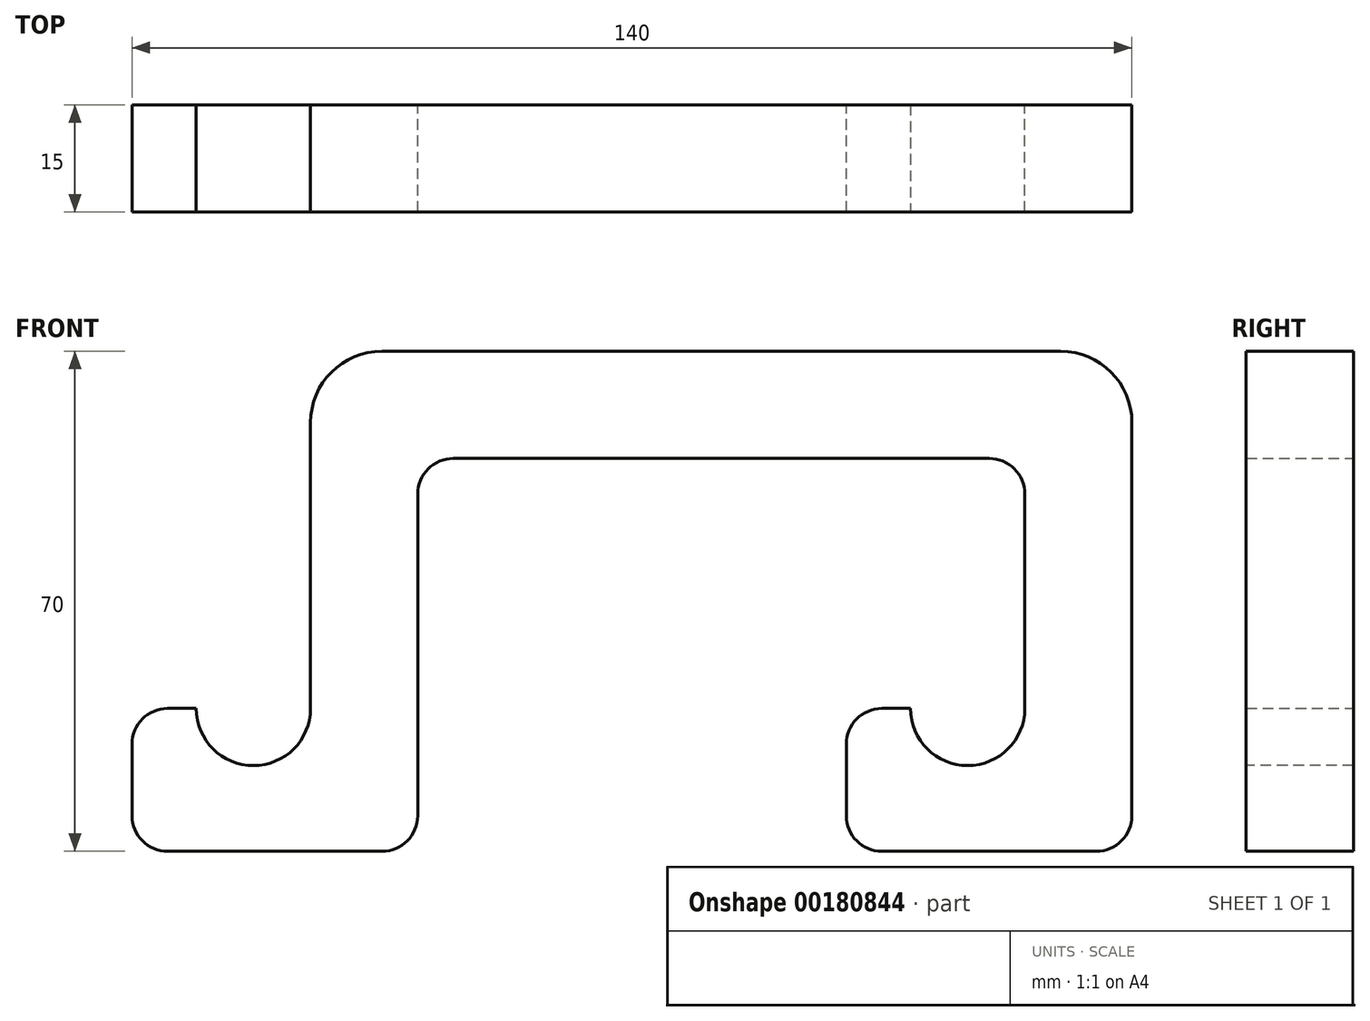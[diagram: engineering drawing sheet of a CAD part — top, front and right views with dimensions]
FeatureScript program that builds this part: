
annotation { "Feature Type Name" : "Feature", "Feature Type Description" : "" }
export const myFeature = defineFeature(function(context is Context, id is Id, definition is map)
    precondition{}
    {
        {
            var Q0;
            Q0=qCreatedBy(makeId("Front.planeOp"),FACE);
            var sketch = newSketch(context, id + "F0", { "sketchPlane" : qUnion([Q0])});
            skLineSegment(sketch, "E0", {"start": v(-64.65, 50) * mm, "end": v(50.35, 50) * mm});
            skLineSegment(sketch, "E1", {"start": v(50.35, 50) * mm, "end": v(50.35, -20) * mm});
            skLineSegment(sketch, "E2", {"start": v(50.35, -20) * mm, "end": v(10.35, -20) * mm});
            skLineSegment(sketch, "E3", {"start": v(10.35, 0) * mm, "end": v(35.35, 0) * mm});
            skLineSegment(sketch, "E4", {"start": v(35.35, 0) * mm, "end": v(35.35, 35) * mm});
            skLineSegment(sketch, "E5", {"start": v(35.35, 35) * mm, "end": v(-49.65, 35) * mm});
            skLineSegment(sketch, "E6", {"start": v(-49.65, 35) * mm, "end": v(-49.65, -20) * mm});
            skLineSegment(sketch, "E7", {"start": v(-49.65, -20) * mm, "end": v(-89.65, -20) * mm});
            skLineSegment(sketch, "E8", {"start": v(-89.65, 0) * mm, "end": v(-64.65, 0) * mm});
            skLineSegment(sketch, "E9", {"start": v(-64.65, 0) * mm, "end": v(-64.65, 50) * mm});
            skLineSegment(sketch, "E10", {"start": v(-89.65, -20) * mm, "end": v(-89.65, 0) * mm});
            skLineSegment(sketch, "E11", {"start": v(10.35, -20) * mm, "end": v(10.35, 0) * mm});
            skSolve(sketch);
        }
        {
            var Q0;
            Q0 = qSketchRegion(id + "F0", true);
            extrude(context, id + "F1", {"entities" : qUnion([Q0]), "depth" : 15 * mm});
        }
        {
            var Q0;
            Q0=makeQuery(id+"F1.opExtrude","CAP_FACE",FACE,{"disambiguationData":[OSD([sQuery(id+"F0.wireOp",EDGE,"E0"),sQuery(id+"F0.wireOp",EDGE,"E1"),sQuery(id+"F0.wireOp",EDGE,"E2"),sQuery(id+"F0.wireOp",EDGE,"aQB5B7aS-mNQQ-RrOO-mPbV-HBg7IGiSB0No"),sQuery(id+"F0.wireOp",EDGE,"0cwBCMxt-gkJu-trWl-BBCZ-zV6T7L2Cuodm"),sQuery(id+"F0.wireOp",EDGE,"ClXoXRWK-djtK-Hku5-tJk9-655eueKnLjd0"),sQuery(id+"F0.wireOp",EDGE,"E3"),sQuery(id+"F0.wireOp",EDGE,"E4"),sQuery(id+"F0.wireOp",EDGE,"E5"),sQuery(id+"F0.wireOp",EDGE,"E6"),sQuery(id+"F0.wireOp",EDGE,"E7"),sQuery(id+"F0.wireOp",EDGE,"e7EVYvR2-Wn0g-ULNJ-eMxn-toWcCi49kqZk"),sQuery(id+"F0.wireOp",EDGE,"T9uqNcK5-KTYk-hCre-gEY8-aIBNllpag4M9"),sQuery(id+"F0.wireOp",EDGE,"z2nKwGSQ-TxCS-aeSP-QmWe-LtRiQycQJufq"),sQuery(id+"F0.wireOp",EDGE,"E8"),sQuery(id+"F0.wireOp",EDGE,"E9")])],"isStart":false});
            var sketch = newSketch(context, id + "F2", { "sketchPlane" : qUnion([Q0])});
            skCircle(sketch, "E12", {"center": v(-72.65, 0) * mm, "radius": 8 * mm});
            skCircle(sketch, "E13", {"center": v(27.35, 0) * mm, "radius": 8 * mm});
            skSolve(sketch);
        }
        {
            var Q0;
            Q0 = qSketchRegion(id + "F2", true);
            extrude(context, id + "F3", {"entities" : qUnion([Q0]), "operationType" : NewBodyOperationType.REMOVE, "endBound" : BoundingType.THROUGH_ALL, "oppositeDirection" : true, "depth" : 25 * mm});
        }
        {
            var Q0;
            Q0=makeQuery(id+"F1.opExtrude","SWEPT_EDGE",EDGE,{"disambiguationData":[OSD([sQuery(id+"F0.wireOp",EDGE,"E0"),sQuery(id+"F0.wireOp",EDGE,"E9")])]});
            var Q1;
            Q1=makeQuery(id+"F1.opExtrude","SWEPT_EDGE",EDGE,{"disambiguationData":[OSD([sQuery(id+"F0.wireOp",EDGE,"E0"),sQuery(id+"F0.wireOp",EDGE,"E1")])]});
            fillet(context, id + "F4", {"entities" : qUnion([Q0, Q1]), "radius" : 10 * mm, "tangentPropagation" : true, "allowEdgeOverflow" : false});
        }
        {
            var Q0;
            Q0=makeQuery(id+"F1.opExtrude","SWEPT_EDGE",EDGE,{"disambiguationData":[OSD([sQuery(id+"F0.wireOp",EDGE,"E8"),sQuery(id+"F0.wireOp",EDGE,"E10")])]});
            var Q1;
            Q1=makeQuery(id+"F1.opExtrude","SWEPT_EDGE",EDGE,{"disambiguationData":[OSD([sQuery(id+"F0.wireOp",EDGE,"E3"),sQuery(id+"F0.wireOp",EDGE,"E11")])]});
            var Q2;
            Q2=makeQuery(id+"F1.opExtrude","SWEPT_EDGE",EDGE,{"disambiguationData":[OSD([sQuery(id+"F0.wireOp",EDGE,"E5"),sQuery(id+"F0.wireOp",EDGE,"E6")])]});
            var Q3;
            Q3=makeQuery(id+"F1.opExtrude","SWEPT_EDGE",EDGE,{"disambiguationData":[OSD([sQuery(id+"F0.wireOp",EDGE,"E4"),sQuery(id+"F0.wireOp",EDGE,"E5")])]});
            fillet(context, id + "F5", {"entities" : qUnion([Q0, Q1, Q2, Q3]), "radius" : 5 * mm, "tangentPropagation" : true, "allowEdgeOverflow" : false});
        }
        {
            var Q0;
            Q0=makeQuery(id+"F1.opExtrude","SWEPT_EDGE",EDGE,{"disambiguationData":[OSD([sQuery(id+"F0.wireOp",EDGE,"E7"),sQuery(id+"F0.wireOp",EDGE,"E10")])]});
            var Q1;
            Q1=makeQuery(id+"F1.opExtrude","SWEPT_EDGE",EDGE,{"disambiguationData":[OSD([sQuery(id+"F0.wireOp",EDGE,"E2"),sQuery(id+"F0.wireOp",EDGE,"E11")])]});
            fillet(context, id + "F6", {"entities" : qUnion([Q0, Q1]), "radius" : 5 * mm, "tangentPropagation" : true, "allowEdgeOverflow" : false});
        }
        {
            var Q0;
            Q0=makeQuery(id+"F1.opExtrude","SWEPT_EDGE",EDGE,{"disambiguationData":[OSD([sQuery(id+"F0.wireOp",EDGE,"E6"),sQuery(id+"F0.wireOp",EDGE,"E7")])]});
            var Q1;
            Q1=makeQuery(id+"F1.opExtrude","SWEPT_EDGE",EDGE,{"disambiguationData":[OSD([sQuery(id+"F0.wireOp",EDGE,"E1"),sQuery(id+"F0.wireOp",EDGE,"E2")])]});
            fillet(context, id + "F7", {"entities" : qUnion([Q0, Q1]), "radius" : 5 * mm, "tangentPropagation" : true, "allowEdgeOverflow" : false});
        }
    });
